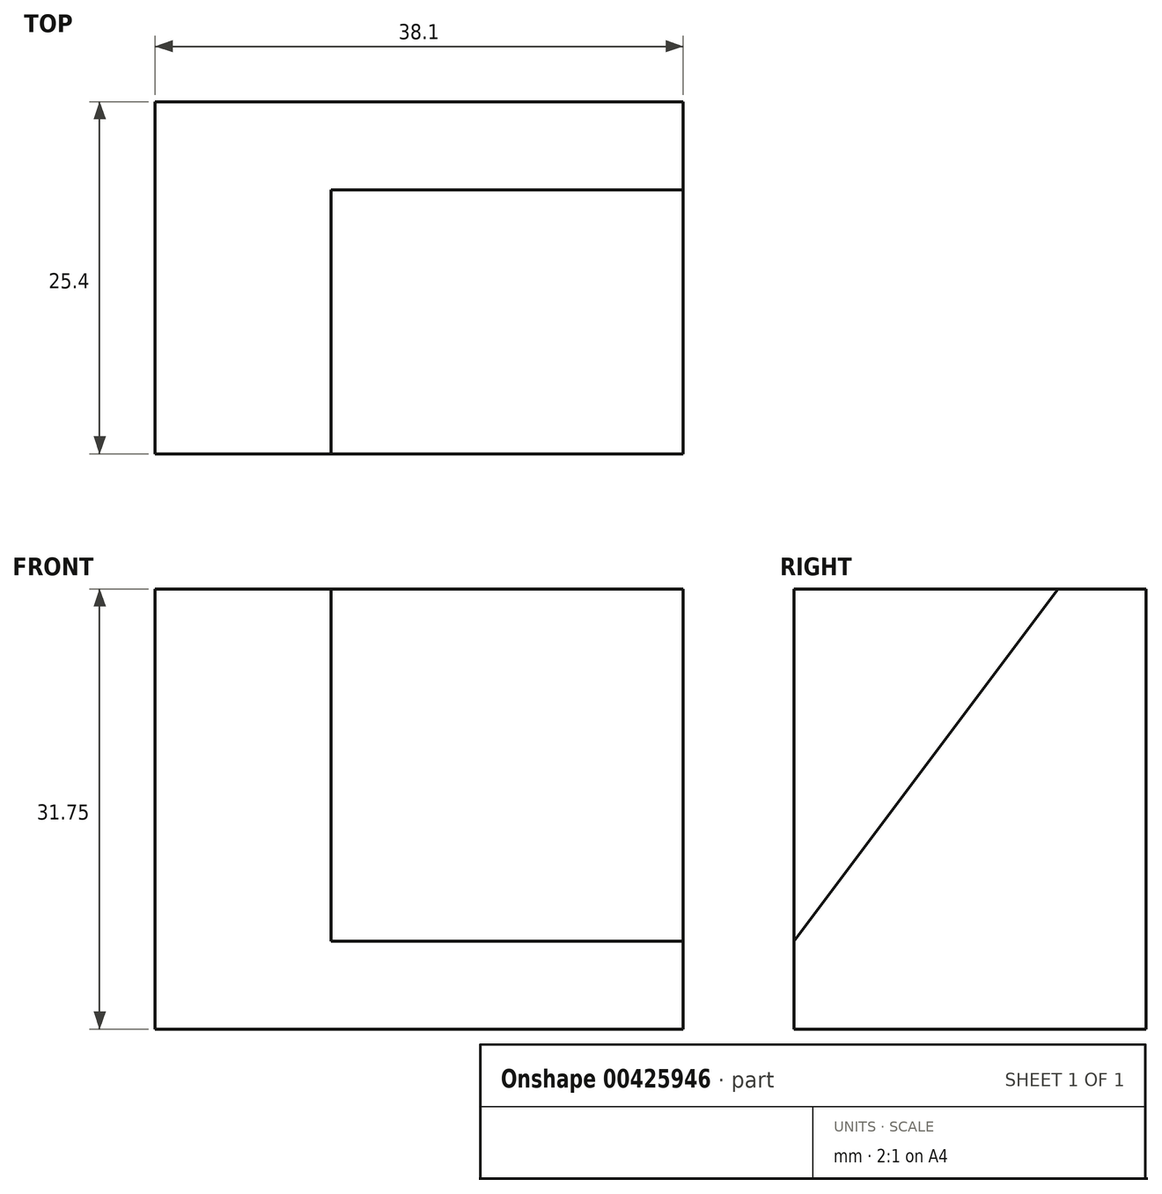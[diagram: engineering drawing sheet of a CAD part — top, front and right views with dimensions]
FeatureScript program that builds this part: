
annotation { "Feature Type Name" : "Feature", "Feature Type Description" : "" }
export const myFeature = defineFeature(function(context is Context, id is Id, definition is map)
    precondition{}
    {
        {
            var Q0;
            Q0=qCreatedBy(makeId("Right.planeOp"),FACE);
            var sketch = newSketch(context, id + "F0", { "sketchPlane" : qUnion([Q0])});
            skLineSegment(sketch, "E0", {"start": v(0, 0) * mm, "end": v(25.4, 0) * mm});
            skLineSegment(sketch, "E1", {"start": v(25.4, 0) * mm, "end": v(25.4, 31.75) * mm});
            skLineSegment(sketch, "E2", {"start": v(0, 0) * mm, "end": v(0, 6.35) * mm});
            skLineSegment(sketch, "E3", {"start": v(25.4, 31.75) * mm, "end": v(19.05, 31.75) * mm});
            skLineSegment(sketch, "E4", {"start": v(0, 6.35) * mm, "end": v(19.05, 31.75) * mm});
            skSolve(sketch);
        }
        {
            var Q0;
            Q0=makeQuery(id+"F0.imprint","IMPRINT",FACE,{"disambiguationData":[TD([[makeQuery(id+"F0.imprint","IMPRINT",EDGE,{"derivedFrom":sQuery(id+"F0.wireOp",EDGE,"E0")}),1.0]])]});
            extrude(context, id + "F1", {"entities" : qUnion([Q0]), "depth" : 25.4 * mm});
        }
        {
            var Q0;
            Q0=qCreatedBy(makeId("Front.planeOp"),FACE);
            var sketch = newSketch(context, id + "F2", { "sketchPlane" : qUnion([Q0])});
            skLineSegment(sketch, "E5", {"start": v(0, 0) * mm, "end": v(-12.7, 0) * mm});
            skLineSegment(sketch, "E6", {"start": v(-12.7, 0) * mm, "end": v(-12.7, 31.75) * mm});
            skLineSegment(sketch, "E7", {"start": v(-12.7, 31.75) * mm, "end": v(0, 31.75) * mm});
            skLineSegment(sketch, "E8", {"start": v(0, 0) * mm, "end": v(0, 31.75) * mm});
            skSolve(sketch);
        }
        {
            var Q0;
            Q0=makeQuery(id+"F2.imprint","IMPRINT",FACE,{"disambiguationData":[TD([[makeQuery(id+"F2.imprint","IMPRINT",EDGE,{"derivedFrom":sQuery(id+"F2.wireOp",EDGE,"E5")}),-1.0]])]});
            extrude(context, id + "F3", {"entities" : qUnion([Q0]), "operationType" : NewBodyOperationType.ADD, "oppositeDirection" : true, "depth" : 25.4 * mm});
        }
    });
